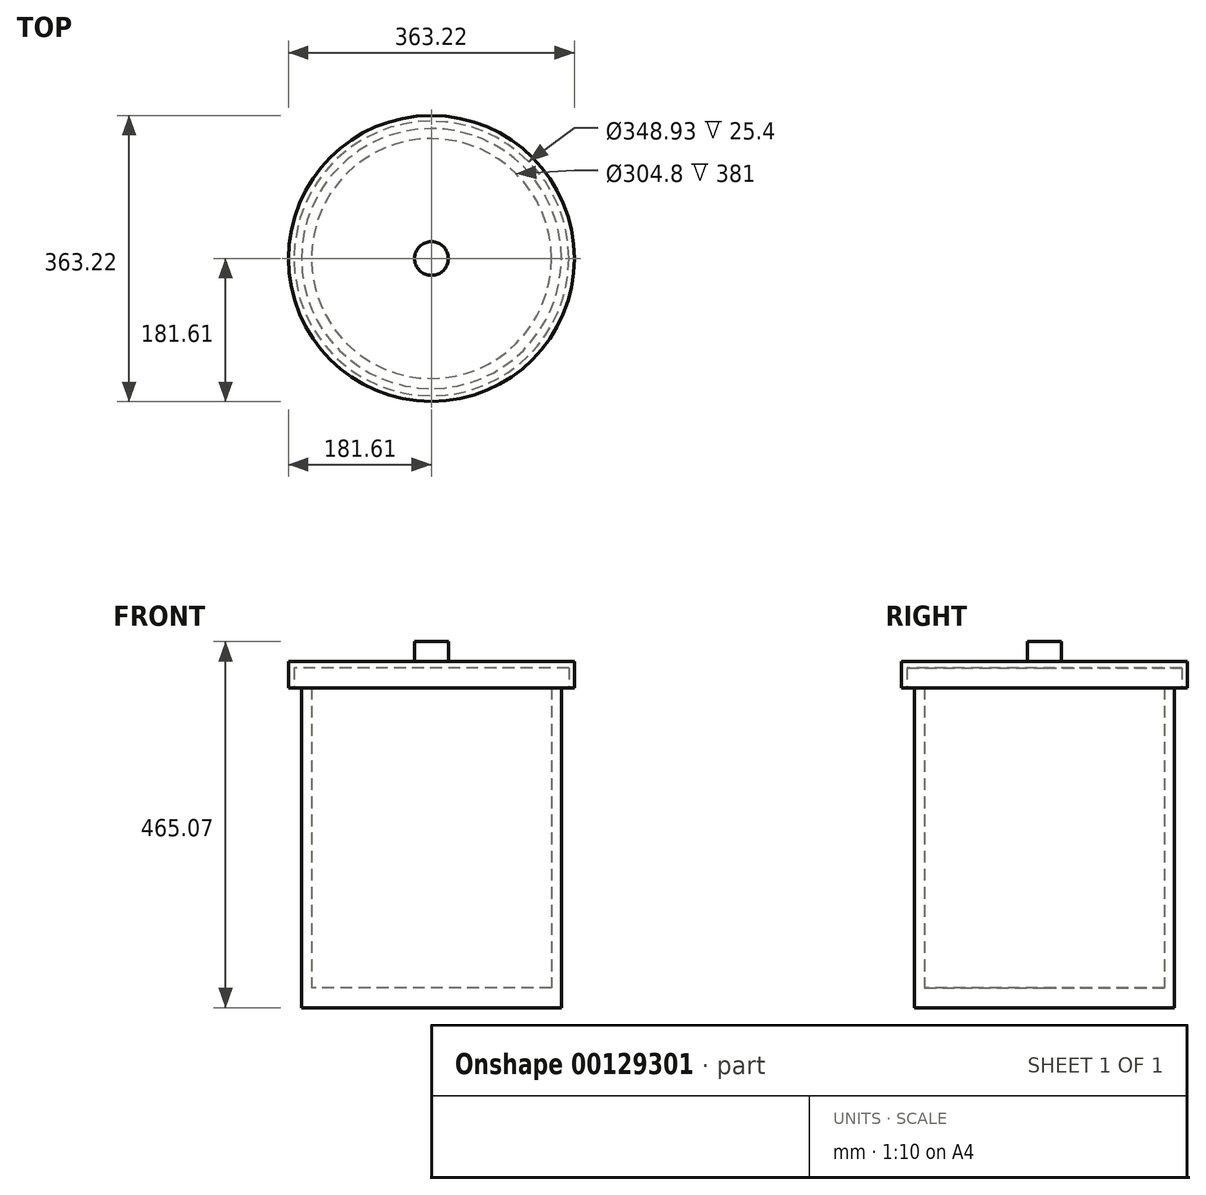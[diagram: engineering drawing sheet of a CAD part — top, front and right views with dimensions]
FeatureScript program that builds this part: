
annotation { "Feature Type Name" : "Feature", "Feature Type Description" : "" }
export const myFeature = defineFeature(function(context is Context, id is Id, definition is map)
    precondition{}
    {
        {
            var Q0;
            Q0=qCreatedBy(makeId("Top.planeOp"),FACE);
            var sketch = newSketch(context, id + "F0", { "sketchPlane" : qUnion([Q0])});
            skCircle(sketch, "E0", {"center": v(0, 0) * mm, "radius": 165.1 * mm});
            skSolve(sketch);
        }
        {
            var Q0;
            Q0 = qSketchRegion(id + "F0", true);
            extrude(context, id + "F1", {"entities" : qUnion([Q0]), "depth" : 25.4 * mm});
        }
        {
            var Q0;
            Q0=makeQuery(id+"F1.opExtrude","CAP_FACE",FACE,{"disambiguationData":[OSD([sQuery(id+"F0.wireOp",EDGE,"E0")])],"isStart":false});
            var sketch = newSketch(context, id + "F2", { "sketchPlane" : qUnion([Q0])});
            skCircle(sketch, "E1", {"center": v(0, 0) * mm, "radius": 165.1 * mm});
            skCircle(sketch, "E2", {"center": v(0, 0) * mm, "radius": 152.4 * mm});
            skSolve(sketch);
        }
        {
            var Q0;
            Q0=makeQuery(id+"F2.imprint","IMPRINT",FACE,{"disambiguationData":[TD([[makeQuery(id+"F2.imprint","IMPRINT",EDGE,{"derivedFrom":sQuery(id+"F2.wireOp",EDGE,"E1")}),1.0]])]});
            extrude(context, id + "F3", {"entities" : qUnion([Q0]), "operationType" : NewBodyOperationType.ADD, "depth" : 381 * mm});
        }
        {
            var Q0;
            Q0=makeQuery(id+"F3.opExtrude","CAP_FACE",FACE,{"disambiguationData":[OSD([sQuery(id+"F2.wireOp",EDGE,"E1"),sQuery(id+"F2.wireOp",EDGE,"E2")])],"isStart":false});
            var sketch = newSketch(context, id + "F4", { "sketchPlane" : qUnion([Q0])});
            skCircle(sketch, "E3", {"center": v(0, 0) * mm, "radius": 174.46 * mm});
            skCircle(sketch, "E4", {"center": v(0, 0) * mm, "radius": 181.61 * mm});
            skSolve(sketch);
        }
        {
            var Q0;
            Q0=makeQuery(id+"F4.imprint","IMPRINT",FACE,{"disambiguationData":[TD([[makeQuery(id+"F4.imprint","IMPRINT",EDGE,{"derivedFrom":sQuery(id+"F4.wireOp",EDGE,"E3")}),-1.0]])]});
            extrude(context, id + "F5", {"entities" : qUnion([Q0]), "depth" : 25.4 * mm});
        }
        {
            var Q0;
            Q0=makeQuery(id+"F5.opExtrude","CAP_FACE",FACE,{"disambiguationData":[OSD([sQuery(id+"F4.wireOp",EDGE,"E3"),sQuery(id+"F4.wireOp",EDGE,"E4")])],"isStart":false});
            var sketch = newSketch(context, id + "F6", { "sketchPlane" : qUnion([Q0])});
            skCircle(sketch, "E5", {"center": v(0, 0) * mm, "radius": 181.61 * mm});
            skSolve(sketch);
        }
        {
            var Q0;
            Q0 = qSketchRegion(id + "F6", true);
            extrude(context, id + "F7", {"entities" : qUnion([Q0]), "operationType" : NewBodyOperationType.ADD, "depth" : 7.87 * mm});
        }
        {
            var Q0;
            Q0=makeQuery(id+"F7.opExtrude","CAP_FACE",FACE,{"disambiguationData":[OSD([sQuery(id+"F6.wireOp",EDGE,"E5")])],"isStart":false});
            var sketch = newSketch(context, id + "F8", { "sketchPlane" : qUnion([Q0])});
            skCircle(sketch, "E6", {"center": v(0, 0) * mm, "radius": 21.46 * mm});
            skSolve(sketch);
        }
        {
            var Q0;
            Q0 = qSketchRegion(id + "F8", true);
            extrude(context, id + "F9", {"entities" : qUnion([Q0]), "operationType" : NewBodyOperationType.ADD, "depth" : 25.4 * mm});
        }
    });
